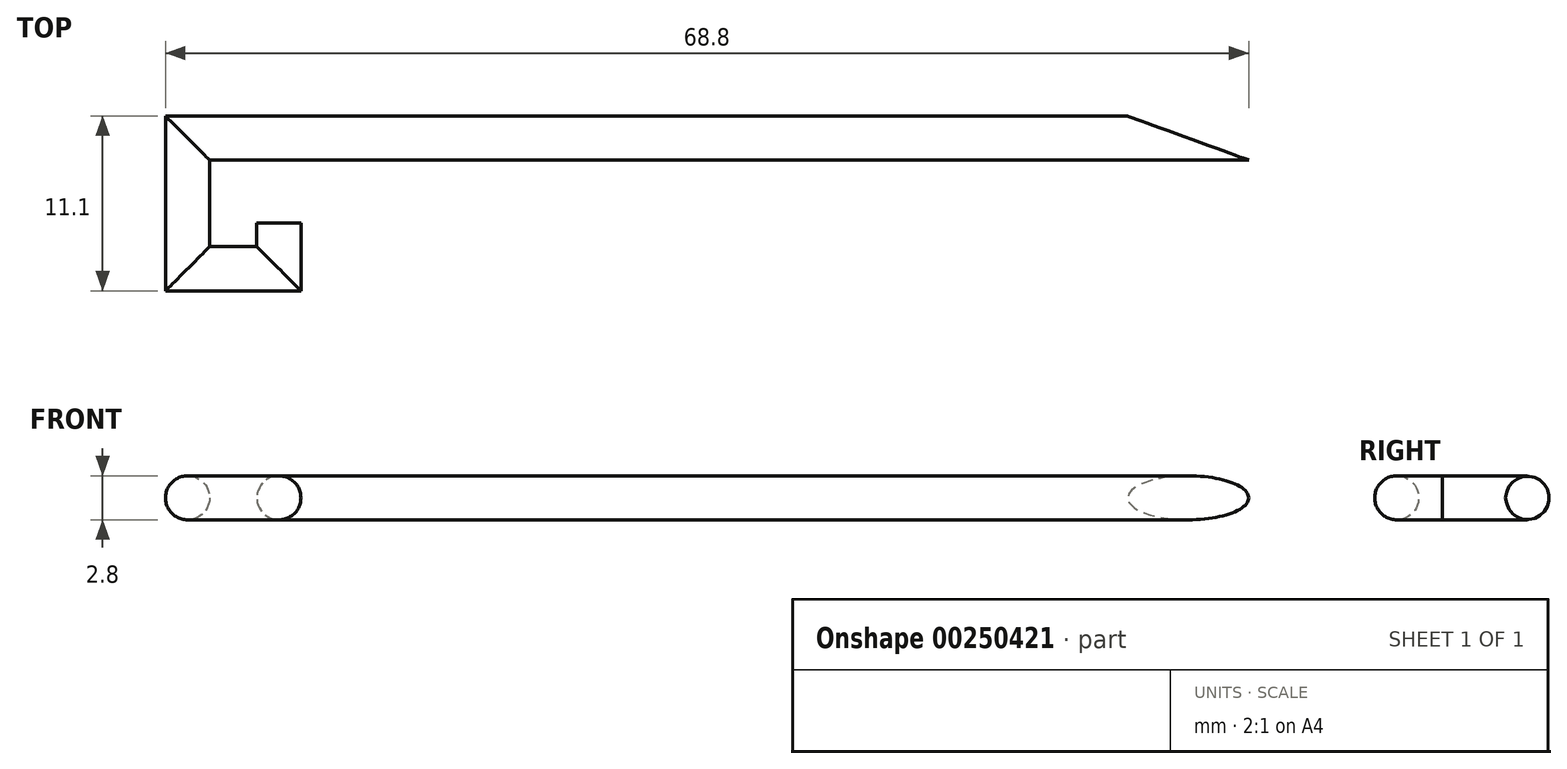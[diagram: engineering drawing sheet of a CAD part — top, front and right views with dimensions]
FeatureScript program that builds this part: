
annotation { "Feature Type Name" : "Feature", "Feature Type Description" : "" }
export const myFeature = defineFeature(function(context is Context, id is Id, definition is map)
    precondition{}
    {
        {
            var Q0;
            Q0=qCreatedBy(makeId("Top.planeOp"),FACE);
            var sketch = newSketch(context, id + "F0", { "sketchPlane" : qUnion([Q0])});
            skLineSegment(sketch, "E0", {"start": v(0, -1.5) * mm, "end": v(0, -3) * mm});
            skLineSegment(sketch, "E1", {"start": v(0, -3) * mm, "end": v(-3, -3) * mm});
            skLineSegment(sketch, "E2", {"start": v(-3, -3) * mm, "end": v(-3, 2.5) * mm});
            skLineSegment(sketch, "E3", {"start": v(-3, 2.5) * mm, "end": v(63, 2.5) * mm});
            skSolve(sketch);
        }
        {
            var Q0;
            Q0=qCreatedBy(makeId("Front.planeOp"),FACE);
            var Q1;
            Q1=sQuery(id+"F0.wireOp",VERTEX,"E0.start");
            cPlane(context, id + "F1", {"entities" : qUnion([Q0, Q1]), "cplaneType" : CPlaneType.PLANE_POINT, "offset" : 25 * mm, "width" : 150 * mm, "height" : 150 * mm});
        }
        {
            var Q0;
            Q0=qCreatedBy(id+"F1.planeOp",FACE);
            var sketch = newSketch(context, id + "F2", { "sketchPlane" : qUnion([Q0])});
            skCircle(sketch, "E4", {"center": v(1.4, 0) * mm, "radius": 1.4 * mm});
            skSolve(sketch);
        }
        {
            var Q0;
            Q0 = qSketchRegion(id + "F2", true);
            var Q1;
            Q1 = qConstructionFilter(qBodyType(qCreatedBy(id + "F0" ,EDGE), BodyType.WIRE), ConstructionObject.NO);
            sweep(context, id + "F3", {"profiles" : qUnion([Q0]), "path" : qUnion([Q1])});
        }
        {
            var Q0;
            Q0=qCreatedBy(makeId("Top.planeOp"),FACE);
            var sketch = newSketch(context, id + "F4", { "sketchPlane" : qUnion([Q0])});
            skLineSegment(sketch, "E5.0", {"start": v(63, 5.3) * mm, "end": v(63, 2.5) * mm});
            skLineSegment(sketch, "E6", {"start": v(63, 5.3) * mm, "end": v(55.3, 5.3) * mm});
            skLineSegment(sketch, "E7", {"start": v(55.3, 5.3) * mm, "end": v(63, 2.5) * mm});
            skSolve(sketch);
        }
        {
            var Q0;
            Q0 = qSketchRegion(id + "F4", true);
            extrude(context, id + "F5", {"entities" : qUnion([Q0]), "operationType" : NewBodyOperationType.REMOVE, "endBound" : BoundingType.SYMMETRIC, "oppositeDirection" : true, "depth" : 25 * mm});
        }
    });
